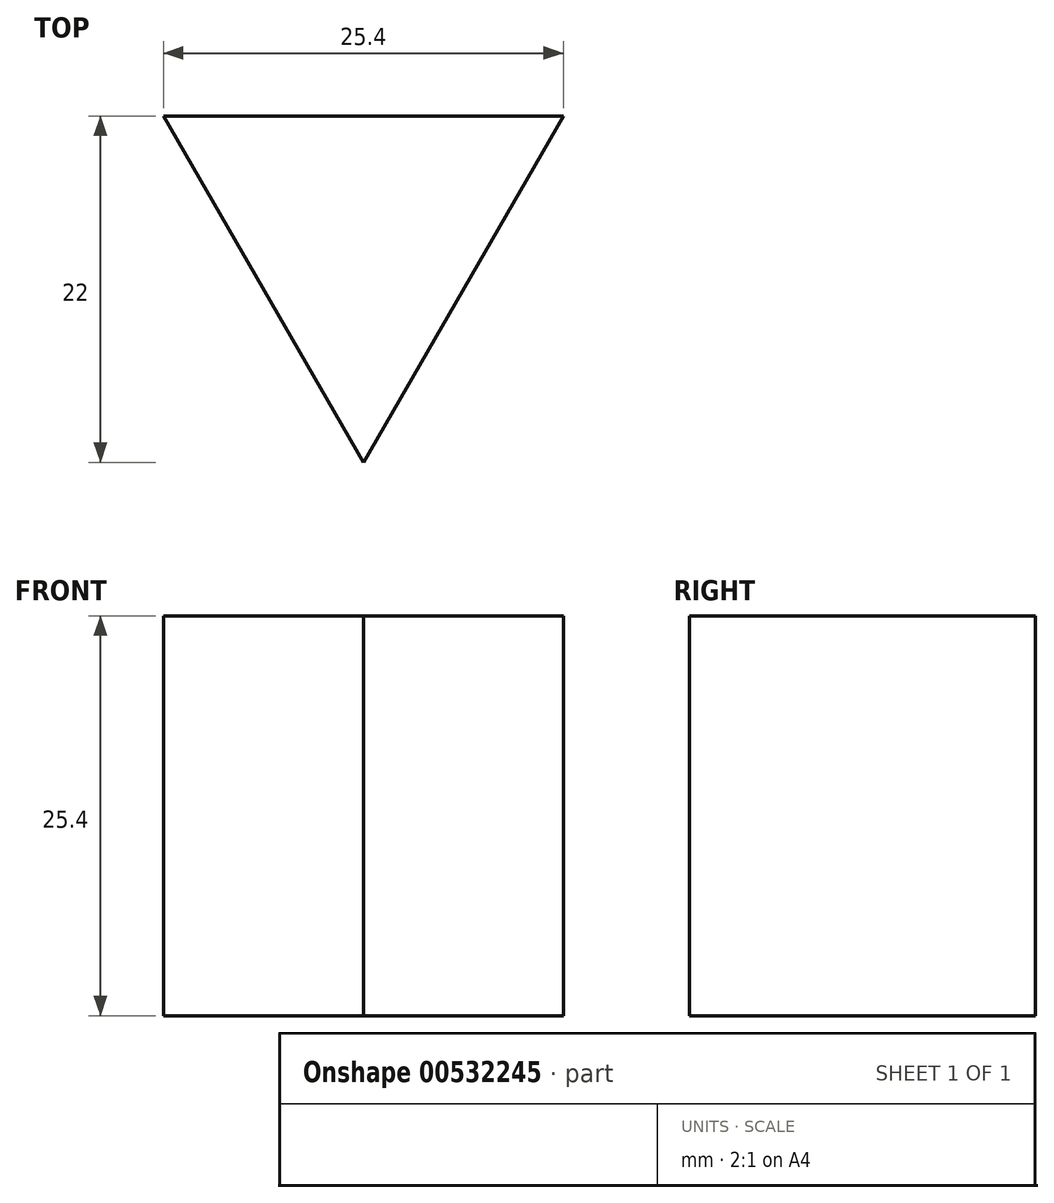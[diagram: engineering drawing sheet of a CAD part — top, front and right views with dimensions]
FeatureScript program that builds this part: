
annotation { "Feature Type Name" : "Feature", "Feature Type Description" : "" }
export const myFeature = defineFeature(function(context is Context, id is Id, definition is map)
    precondition{}
    {
        {
            var Q0;
            Q0=qCreatedBy(makeId("Top.planeOp"),FACE);
            var sketch = newSketch(context, id + "F0", { "sketchPlane" : qUnion([Q0])});
            skLineSegment(sketch, "E0", {"start": v(0, 0) * mm, "end": v(-12.7, 22) * mm});
            skLineSegment(sketch, "E1", {"start": v(-12.7, 22) * mm, "end": v(12.7, 22) * mm});
            skLineSegment(sketch, "E2", {"start": v(12.7, 22) * mm, "end": v(0, 0) * mm});
            skSolve(sketch);
        }
        {
            var Q0;
            Q0 = qSketchRegion(id + "F0", true);
            extrude(context, id + "F1", {"entities" : qUnion([Q0]), "depth" : 25.4 * mm, "offsetDistance" : 25.4 * mm});
        }
    });
